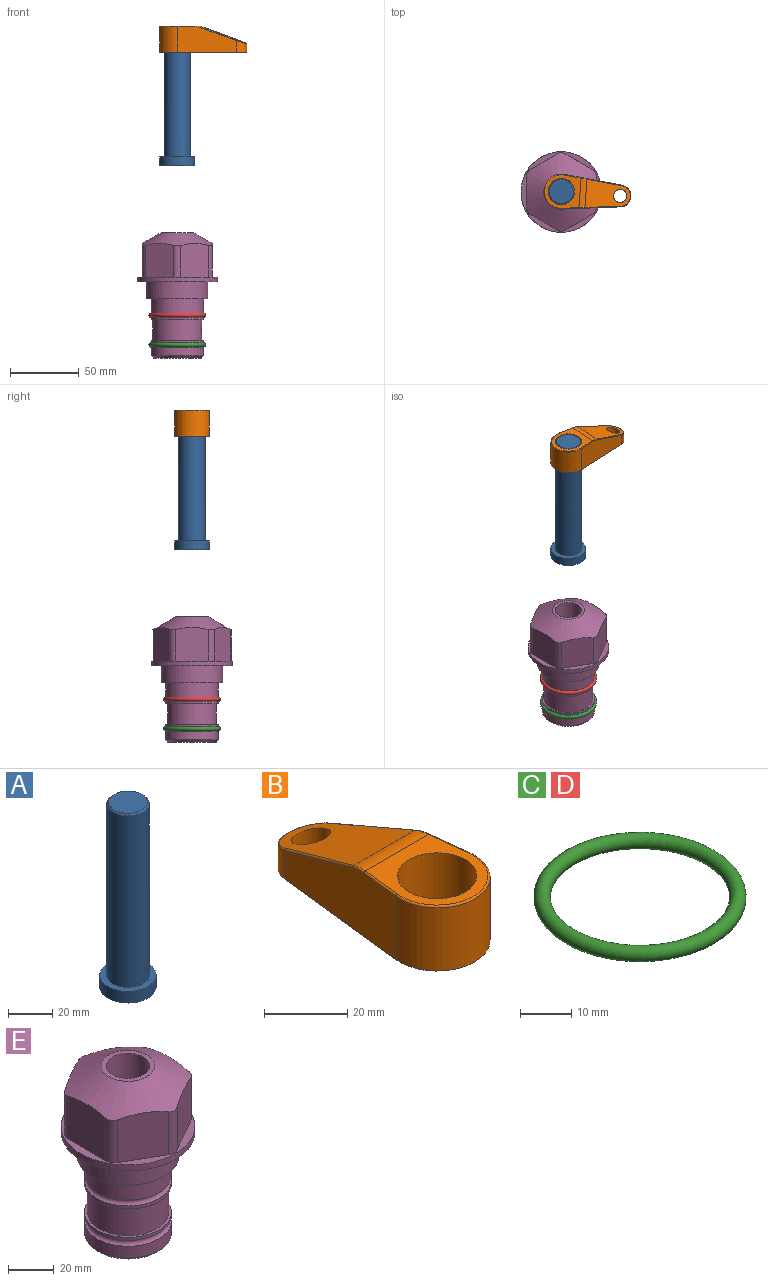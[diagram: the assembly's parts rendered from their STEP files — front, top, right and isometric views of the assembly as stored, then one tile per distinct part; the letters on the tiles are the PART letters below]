
ASSEMBLY  parts=5 mates=3
PART A: 6 faces, bbox 25.4x25.4x101.6 mm
  f0: plane 17.46x17.46mm, normal (0,0,1), area 239.5mm2, adj f5
  f1: plane 25.4x25.4mm, normal (0,0,-1), area 506.7mm2, adj f2
  f2: cylinder r=12.7mm len=25.4mm, axis (0,0,1), area 506.7mm2, adj f1,f3
  f3: plane 25.4x25.4mm, normal (0,0,1), area 221.7mm2, adj f2,f4
  f4: cylinder r=9.53mm len=94.46mm, axis (0,0,1), area 5653mm2, adj f3,f5
  f5: cone r=8.73mm half-angle=45deg, axis (0,0,-1), area 64.4mm2, adj f0,f4
PART B: 44 faces, bbox 27.5x64.5x19.1 mm
  f0: plane 2.3x0.95mm, normal (0,0,-1), area 1mm2, adj f25,f30,f34
  f1: plane 63.5x25.4mm, normal (0,0,-1), area 561.7mm2, adj f2,f3,f4,f5,f6,f7,f19,f20
  f2: cylinder r=12.7mm len=25.4mm, axis (0,0,-1), area 792.2mm2, adj f1,f3,f5,f13
  f3: plane 42.33x18.54mm, normal (0.99,0.11,0), area 647mm2, adj f1,f2,f4,f11,f12,f14
  f4: cylinder r=7.94mm len=15.78mm, axis (0,0,-1), area 158.6mm2, adj f1,f3,f5,f16
  f5: plane 42.33x18.54mm, normal (-0.99,0.11,0), area 647mm2, adj f1,f2,f4,f15,f17,f18
  f6: cylinder r=9.53mm len=19.05mm, axis (0,0,-1), area 1140.1mm2, adj f1,f8
  f7: cylinder r=4.76mm len=10.98mm, axis (0,0,-1), area 276.1mm2, adj f1,f9
  f8: plane 25.83x24.38mm, normal (0,0,1), area 262.2mm2, adj f6,f10,f11,f13,f15
  f9: plane 32.49x20.55mm, normal (0,0.34,0.94), area 489.9mm2, adj f7,f10,f14,f16,f18
  f10: cylinder r=12.7mm len=21.49mm, axis (-1,0,0), area 93.2mm2, adj f8,f9,f12,f17
  f11: cylinder r=0.51mm len=12.34mm, axis (0.11,-0.99,0), area 9.9mm2, adj f3,f8,f12,f13
  f12: bspline ~7.62x1.64mm, area 3.5mm2, adj f3,f10,f11,f14
  f13: torus R=12.19mm, axis (0,0,1), area 33.6mm2, adj f2,f8,f11,f15
  f14: cylinder r=0.51mm len=26.01mm, axis (0.1,-0.93,0.34), area 21.6mm2, adj f3,f9,f12,f16
  f15: cylinder r=0.51mm len=12.34mm, axis (0.11,0.99,0), area 9.9mm2, adj f5,f8,f13,f17
  f16: bspline ~15.78x7.05mm, area 15.7mm2, adj f4,f9,f14,f18
  f17: bspline ~7.62x1.64mm, area 3.5mm2, adj f5,f10,f15,f18
  f18: cylinder r=0.51mm len=26.01mm, axis (0.1,0.93,-0.34), area 21.6mm2, adj f5,f9,f16,f17
  f19: plane 21.6x14.29mm, normal (-0.99,-0.11,0), area 242.6mm2, adj f1,f26,f28,f34,f36,f38
  f20: plane 21.6x14.29mm, normal (0.99,-0.11,0), area 242.6mm2, adj f1,f27,f29,f37,f39,f41
  f21: cylinder r=12.7mm len=14.29mm, axis (0,0,-1), area 173.2mm2, adj f1,f26,f27,f30,f31,f33
  f22: cylinder r=7.94mm len=7.63mm, axis (0,0,-1), area 53.8mm2, adj f1,f28,f29,f42
  f23: plane 2.3x0.95mm, normal (0,0,-1), area 1mm2, adj f25,f33,f37
  f24: plane 17.94x12.32mm, normal (0,-0.34,-0.94), area 191.2mm2, adj f25,f38,f41,f42
  f25: cylinder r=9.53mm len=12.93mm, axis (-1,0,0), area 37.5mm2, adj f0,f23,f24,f31,f36,f39
  f26: cylinder r=1.59mm len=14.29mm, axis (0,0,-1), area 49mm2, adj f1,f19,f21,f32
  f27: cylinder r=1.59mm len=14.29mm, axis (0,0,-1), area 49mm2, adj f1,f20,f21,f35
  f28: cylinder r=1.59mm len=7.28mm, axis (0,0,-1), area 22.1mm2, adj f1,f19,f22,f40
  f29: cylinder r=1.59mm len=7.28mm, axis (0,0,-1), area 22.1mm2, adj f1,f20,f22,f43
  f30: torus R=14.29mm, axis (0,0,1), area 5.8mm2, adj f0,f21,f31,f32
  f31: bspline ~11.06x2.73mm, area 20.8mm2, adj f21,f25,f30,f33
  f32: sphere r=1.59mm, area 5.4mm2, adj f26,f30,f34
  f33: torus R=14.29mm, axis (0,0,1), area 5.8mm2, adj f21,f23,f31,f35
  f34: cylinder r=1.59mm len=1.68mm, axis (-0.11,0.99,0), area 2.4mm2, adj f0,f19,f32,f36
  f35: sphere r=1.59mm, area 5.4mm2, adj f27,f33,f37
  f36: bspline ~5.82x2.33mm, area 7.7mm2, adj f19,f25,f34,f38
  f37: cylinder r=1.59mm len=1.68mm, axis (0.11,0.99,0), area 2.4mm2, adj f20,f23,f35,f39
  f38: cylinder r=1.59mm len=18.33mm, axis (0.1,-0.93,0.34), area 46.7mm2, adj f19,f24,f36,f40
  f39: bspline ~5.82x2.33mm, area 7.7mm2, adj f20,f25,f37,f41
  f40: sphere r=1.59mm, area 3.6mm2, adj f28,f38,f42
  f41: cylinder r=1.59mm len=18.33mm, axis (0.1,0.93,-0.34), area 46.7mm2, adj f20,f24,f39,f43
  f42: bspline ~8.31x1.84mm, area 15.3mm2, adj f22,f24,f40,f43
  f43: sphere r=1.59mm, area 3.6mm2, adj f29,f41,f42
PART C: 1 faces, bbox 44.7x44.7x3.2 mm
  f0: torus R=19.05mm, axis (0,0,1), area 1193.9mm2
PART D: same geometry as C
PART E: 36 faces, bbox 58.7x58.7x91.2 mm
  f0: cylinder r=17.78mm len=35.56mm, axis (0,0,1), area 1670.8mm2, adj f23,f24,f31
  f1: cylinder r=19.05mm len=38.1mm, axis (0,0,1), area 1191.9mm2, adj f26,f27,f30
  f2: plane 58.66x58.66mm, normal (0,0,-1), area 1150.6mm2, adj f3,f28
  f3: cylinder r=29.33mm len=58.66mm, axis (0,0,-1), area 585.1mm2, adj f2,f4
  f4: plane 58.66x58.66mm, normal (0,0,1), area 475.9mm2, adj f3,f5,f6,f7,f8,f9,f10,f11
  f5: plane 24.5x20.32mm, normal (-0.5,0.87,0), area 562.8mm2, adj f4,f15,f16,f17
  f6: plane 24.5x20.32mm, normal (0.5,0.87,0), area 562.8mm2, adj f4,f14,f15,f17
  f7: plane 24.5x23.48mm, normal (1,0,0), area 562.8mm2, adj f4,f13,f14,f17
  f8: plane 24.5x20.32mm, normal (0.5,-0.87,0), area 562.8mm2, adj f4,f12,f13,f17
  f9: plane 24.5x20.32mm, normal (-0.5,-0.87,0), area 562.8mm2, adj f4,f11,f12,f17
  f10: plane 24.5x23.48mm, normal (-1,0,0), area 562.8mm2, adj f4,f11,f16,f17
  f11: cylinder r=5.08mm len=23.01mm, axis (0,0,-1), area 121.2mm2, adj f4,f9,f10,f17
  f12: cylinder r=5.08mm len=23.01mm, axis (0,0,-1), area 121.2mm2, adj f4,f8,f9,f17
  f13: cylinder r=5.08mm len=23.01mm, axis (0,0,-1), area 121.2mm2, adj f4,f7,f8,f17
  f14: cylinder r=5.08mm len=23.01mm, axis (0,0,-1), area 121.2mm2, adj f4,f6,f7,f17
  f15: cylinder r=5.08mm len=23.01mm, axis (0,0,-1), area 121.2mm2, adj f4,f5,f6,f17
  f16: cylinder r=5.08mm len=23.01mm, axis (0,0,-1), area 121.2mm2, adj f4,f5,f10,f17
  f17: cone r=11.73mm half-angle=60deg, axis (0,0,-1), area 2071.8mm2, adj f5,f6,f7,f8,f9,f10,f11,f12
  f18: plane 23.46x23.46mm, normal (0,0,1), area 147.4mm2, adj f17,f35
  f19: plane 34.93x34.93mm, normal (0,0,-1), area 958mm2, adj f29
  f20: cylinder r=19.05mm len=38.1mm, axis (0,0,1), area 760.1mm2, adj f21,f29
  f21: torus R=19.05mm, axis (0,0,1), area 565.3mm2, adj f20,f22
  f22: cylinder r=19.05mm len=38.1mm, axis (0,0,1), area 190mm2, adj f21,f23
  f23: plane 38.1x38.1mm, normal (0,0,1), area 146.9mm2, adj f0,f22
  f24: plane 38.1x38.1mm, normal (0,0,-1), area 146.9mm2, adj f0,f25
  f25: cylinder r=19.05mm len=38.1mm, axis (0,0,1), area 190mm2, adj f24,f26
  f26: torus R=19.05mm, axis (0,0,1), area 565.3mm2, adj f1,f25
  f27: plane 44.45x44.45mm, normal (0,0,-1), area 411.7mm2, adj f1,f28
  f28: cylinder r=22.23mm len=44.45mm, axis (0,0,1), area 1773.5mm2, adj f2,f27
  f29: cone r=19.05mm half-angle=45deg, axis (0,0,1), area 257.5mm2, adj f19,f20
  f30: cylinder r=3.17mm len=6.75mm, axis (-1,0,0), area 128mm2, adj f1,f33
  f31: cylinder r=3.17mm len=6.35mm, axis (-1,0,0), area 102.5mm2, adj f0,f33
  f32: plane 25.4x25.4mm, normal (0,0,1), area 506.7mm2, adj f33
  f33: cylinder r=12.7mm len=66.42mm, axis (0,0,-1), area 5236.2mm2, adj f30,f31,f32,f34
  f34: cone r=9.53mm half-angle=30deg, axis (0,0,-1), area 443.4mm2, adj f33,f35
  f35: cylinder r=9.53mm len=19.05mm, axis (0,0,-1), area 849mm2, adj f18,f34
PLACE A rot(axis=(0,0,-1),4.2deg) t=(0,0,112.16)mm
PLACE B rot(axis=(0,0,-1),94.2deg) t=(0,0,166.77)mm
PLACE C t=(0,0,-21.59)mm
PLACE D at identity
PLACE E at identity fixed
MATE fastened C.f0 <-> E.f0  axis (0,0,1) through (0,0,-46.1)mm
MATE cylindrical A.f2 <-> E.f0  axis (0,0,1) through (0,0,137.79)mm
MATE fastened B.f2 <-> A.f2  axis (0,0,1) through (0,0,185.82)mm
